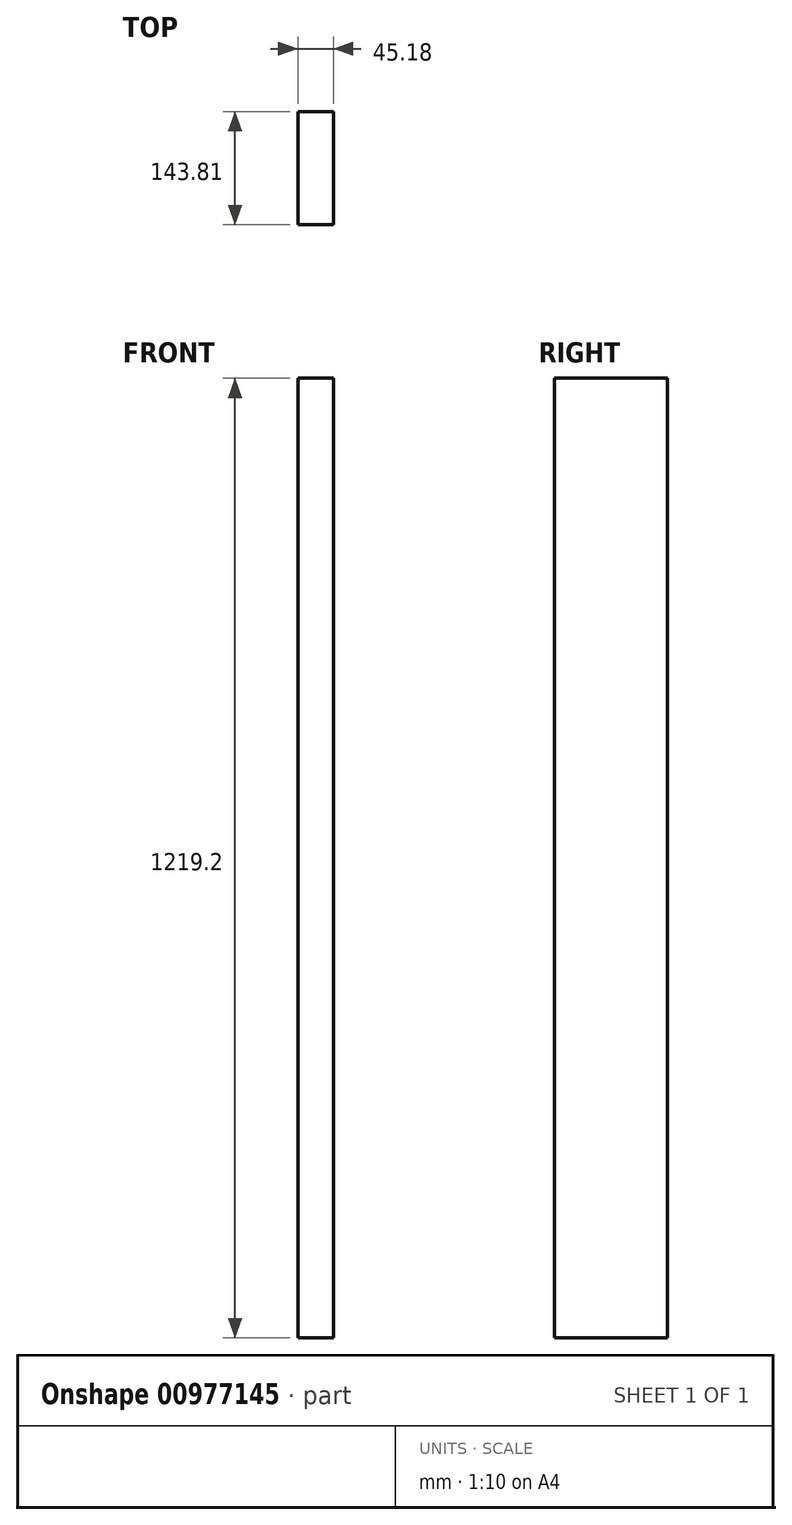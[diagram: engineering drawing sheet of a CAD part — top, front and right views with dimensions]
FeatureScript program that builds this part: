
annotation { "Feature Type Name" : "Feature", "Feature Type Description" : "" }
export const myFeature = defineFeature(function(context is Context, id is Id, definition is map)
    precondition{}
    {
        {
            var Q0;
            Q0=qCreatedBy(makeId("Top.planeOp"),FACE);
            var sketch = newSketch(context, id + "F0", { "sketchPlane" : qUnion([Q0])});
            skLineSegment(sketch, "E0", {"start": v(-46.32, 120.6) * mm, "end": v(-46.32, -23.2) * mm});
            skLineSegment(sketch, "E1", {"start": v(-46.32, -23.2) * mm, "end": v(-1.14, -23.2) * mm});
            skLineSegment(sketch, "E2", {"start": v(-1.14, -23.2) * mm, "end": v(-1.14, 120.6) * mm});
            skLineSegment(sketch, "E3", {"start": v(-1.14, 120.6) * mm, "end": v(-46.32, 120.6) * mm});
            skSolve(sketch);
        }
        {
            var Q0;
            Q0=makeQuery(id+"F0.imprint","IMPRINT",FACE,{"disambiguationData":[TD([[makeQuery(id+"F0.imprint","IMPRINT",EDGE,{"derivedFrom":sQuery(id+"F0.wireOp",EDGE,"E0")}),1.0]])]});
            extrude(context, id + "F1", {"entities" : qUnion([Q0]), "depth" : 1219.2 * mm, "offsetDistance" : 25.4 * mm});
        }
    });
